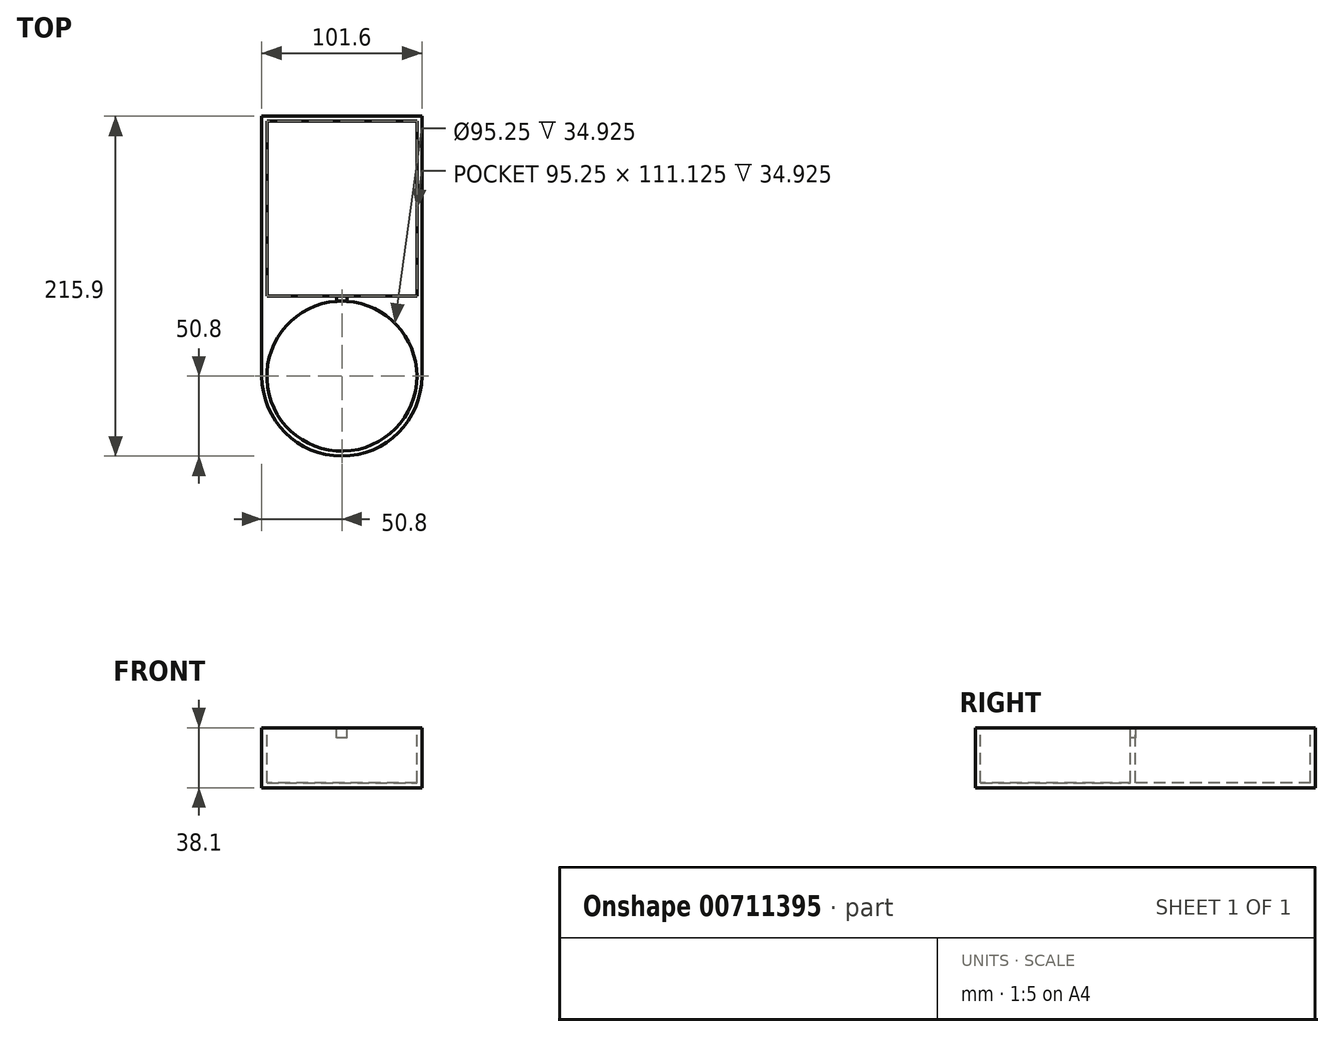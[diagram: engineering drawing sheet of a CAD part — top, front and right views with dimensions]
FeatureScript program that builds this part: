
annotation { "Feature Type Name" : "Feature", "Feature Type Description" : "" }
export const myFeature = defineFeature(function(context is Context, id is Id, definition is map)
    precondition{}
    {
        {
            var Q0;
            Q0=qCreatedBy(makeId("Top.planeOp"),FACE);
            var sketch = newSketch(context, id + "F0", { "sketchPlane" : qUnion([Q0])});
            skArc(sketch, "E0", {"start": v(-50.8, 0) * mm, "mid": v(0, -50.8) * mm, "end": v(50.8, 0) * mm});
            skLineSegment(sketch, "E1.bottom", {"start": v(-50.8, 0) * mm, "end": v(50.8, 0) * mm});
            skLineSegment(sketch, "E1.top", {"start": v(-50.8, 165.1) * mm, "end": v(50.8, 165.1) * mm});
            skLineSegment(sketch, "E1.left", {"start": v(-50.8, 0) * mm, "end": v(-50.8, 165.1) * mm});
            skLineSegment(sketch, "E1.right", {"start": v(50.8, 0) * mm, "end": v(50.8, 165.1) * mm});
            skSolve(sketch);
        }
        {
            var Q0;
            Q0 = qSketchRegion(id + "F0", true);
            extrude(context, id + "F1", {"entities" : qUnion([Q0]), "depth" : 38.1 * mm, "offsetDistance" : 25.4 * mm});
        }
        {
            var Q0;
            Q0=makeQuery(id+"F1.opExtrude","CAP_FACE",FACE,{"disambiguationData":[OSD([sQuery(id+"F0.wireOp",EDGE,"E0"),sQuery(id+"F0.wireOp",EDGE,"E1.top"),sQuery(id+"F0.wireOp",EDGE,"E1.left"),sQuery(id+"F0.wireOp",EDGE,"E1.right")])],"isStart":false});
            var sketch = newSketch(context, id + "F2", { "sketchPlane" : qUnion([Q0])});
            skCircle(sketch, "E2", {"center": v(0, 0) * mm, "radius": 47.63 * mm});
            skSolve(sketch);
        }
        {
            var Q0;
            Q0 = qSketchRegion(id + "F2", true);
            extrude(context, id + "F3", {"entities" : qUnion([Q0]), "operationType" : NewBodyOperationType.REMOVE, "oppositeDirection" : true, "depth" : 34.92 * mm, "offsetDistance" : 25.4 * mm});
        }
        {
            var Q0;
            Q0=qCreatedBy(makeId("Front.planeOp"),FACE);
            var sketch = newSketch(context, id + "F4", { "sketchPlane" : qUnion([Q0])});
            skLineSegment(sketch, "E3.bottom", {"start": v(3.17, 38.1) * mm, "end": v(-3.18, 38.1) * mm});
            skLineSegment(sketch, "E3.top", {"start": v(3.18, 31.75) * mm, "end": v(-3.17, 31.75) * mm});
            skLineSegment(sketch, "E3.left", {"start": v(3.18, 38.1) * mm, "end": v(3.18, 31.75) * mm});
            skLineSegment(sketch, "E3.right", {"start": v(-3.18, 38.1) * mm, "end": v(-3.17, 31.75) * mm});
            skPoint(sketch, "E3.middle", {"position": v(0, 34.92) * mm});
            skSolve(sketch);
        }
        {
            var Q0;
            Q0 = qSketchRegion(id + "F4", true);
            extrude(context, id + "F5", {"entities" : qUnion([Q0]), "operationType" : NewBodyOperationType.REMOVE, "oppositeDirection" : true, "depth" : 50.8 * mm, "offsetDistance" : 25.4 * mm});
        }
        {
            var Q0;
            Q0=makeQuery(id+"F1.opExtrude","CAP_FACE",FACE,{"disambiguationData":[OSD([sQuery(id+"F0.wireOp",EDGE,"E0"),sQuery(id+"F0.wireOp",EDGE,"E1.top"),sQuery(id+"F0.wireOp",EDGE,"E1.left"),sQuery(id+"F0.wireOp",EDGE,"E1.right")])],"isStart":false});
            var sketch = newSketch(context, id + "F6", { "sketchPlane" : qUnion([Q0])});
            skLineSegment(sketch, "E4.bottom", {"start": v(-47.63, 161.93) * mm, "end": v(47.62, 161.93) * mm});
            skLineSegment(sketch, "E4.top", {"start": v(-47.63, 50.8) * mm, "end": v(47.62, 50.8) * mm});
            skLineSegment(sketch, "E4.left", {"start": v(-47.63, 161.93) * mm, "end": v(-47.63, 50.8) * mm});
            skLineSegment(sketch, "E4.right", {"start": v(47.62, 161.93) * mm, "end": v(47.62, 50.8) * mm});
            skSolve(sketch);
        }
        {
            var Q0;
            Q0 = qSketchRegion(id + "F6", true);
            extrude(context, id + "F7", {"entities" : qUnion([Q0]), "operationType" : NewBodyOperationType.REMOVE, "oppositeDirection" : true, "depth" : 34.92 * mm, "offsetDistance" : 25.4 * mm});
        }
    });
